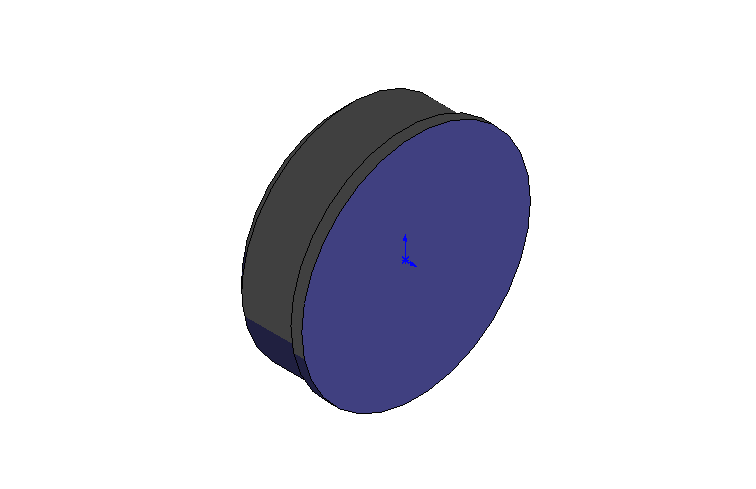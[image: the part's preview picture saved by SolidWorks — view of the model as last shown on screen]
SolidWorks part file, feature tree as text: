
SOLIDWORKS PART (.sldprt)
format: sldprt  version: not decoded by parser v0  size: 93,184 bytes
history: native  units: mm
features: plane x3, sketch x2, extrude x2, material x1, chamfer x1 (+10 scaffold rows collapsed)
feature tree (19):
  scaffold x10  (default folders/planes/origin — collapsed)
  material  "Matériau <non spécifié>"
  plane  "Plan de face"
  plane  "Plan de dessus"
  plane  "Plan de droite"
  sketch  "Esquisse1"  dims[D1=21.0mm]
  extrude  "Extrusion1"  Depth=1mm
  sketch  "Esquisse2"  dims[c1.D1=20.0mm c1.D2=15.5mm c2.D1=20.0mm c2.D2=15.5mm]
  extrude  "Extrusion2"  Depth=6mm
  chamfer  "Chanfrein1"  Distance=1mm Angle=45deg
decode coverage: 5 of 5 modeling features carry decoded parameters
note: suppression state not decoded; provenance and decode notes live in map.json
